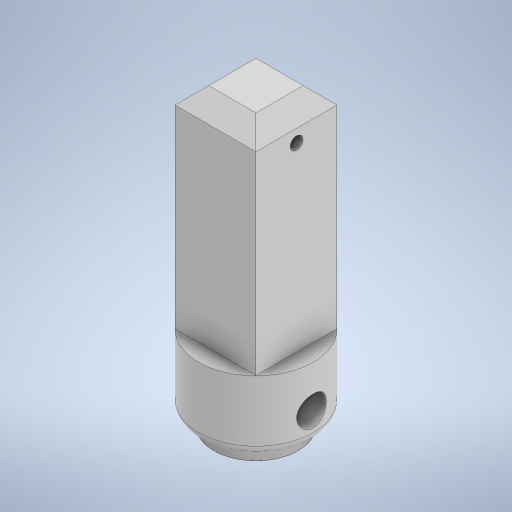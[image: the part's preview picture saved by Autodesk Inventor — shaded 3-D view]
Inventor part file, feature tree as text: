
AUTODESK INVENTOR PART (.ipt)
format: ipt  version: 2024.2 (Build 282272000, 272)  size: 303,104 bytes
history: native  units: mm
features: sketch x6, extrude x4, hole x2, fillet x2, chamfer x1
ambient origin geometry x8: Origin, YZ Plane, XZ Plane, XY Plane, X Axis, Y Axis, Z Axis, Center Point
bodies: Solid1 (feature_tree)
feature tree (15):
  extrude  "Extrusion1"  Depth=9.6mm
  extrude  "Extrusion5"  Depth=3.5mm
  hole  "Hole1"  [1 undecoded]
  extrude  "Extrusion7"  Depth=5.0mm
  hole  "Hole3"  [1 undecoded]
  extrude  "Extrusion8"  Depth=10.0mm
  fillet  "Fillet3"  Radius=2.0mm
  chamfer  "Chamfer1"  Distance=2.0mm
  fillet  "Fillet5"  Radius=2.0mm
  sketch  "Sketch1"  dims[d0=9.6mm d1=9.6mm]
  sketch  "Sketch5"  dims[d2=35.0mm d3=0.0mm d14=3.5mm]
  sketch  "Sketch6"  dims[d15=10.0mm d16=0.0mm d18=3.5mm]
  sketch  "Sketch9"  dims[d19=1.5mm d20=6.0mm d21=4.0mm d22=2.0mm d23=90.0deg d24=8.0mm d25=20.594885mm d41=5.0mm]
  sketch  "Sketch10"  dims[d42=3.5mm d43=5.0mm d44=4.0mm d45=0.0mm d46=0.0mm]
  sketch  "Sketch11"  dims[d47=3.5mm d48=6.0mm d49=4.0mm d50=2.0mm d51=90.0deg d52=9.0mm d53=20.594885mm d55=10.0mm d56=2.0mm d57=0.0mm d58=2.0mm d60=2.0mm d61=2.0mm d62=45.0deg d63=15.0mm d64=1.0mm d65=1.0mm d66=1.0mm d67=0.15mm d68=3.5mm d69=0.375mm d70=14.3117mm d71=0.75mm d72=20.594885mm d73=0.0625mm d74=0.75mm d75=0.375mm]
note: 2 required parameter values undecoded (feature->parameter linkage not recoverable at this tier; creation-order binding heuristic only, values carry confidence <= 0.55)
